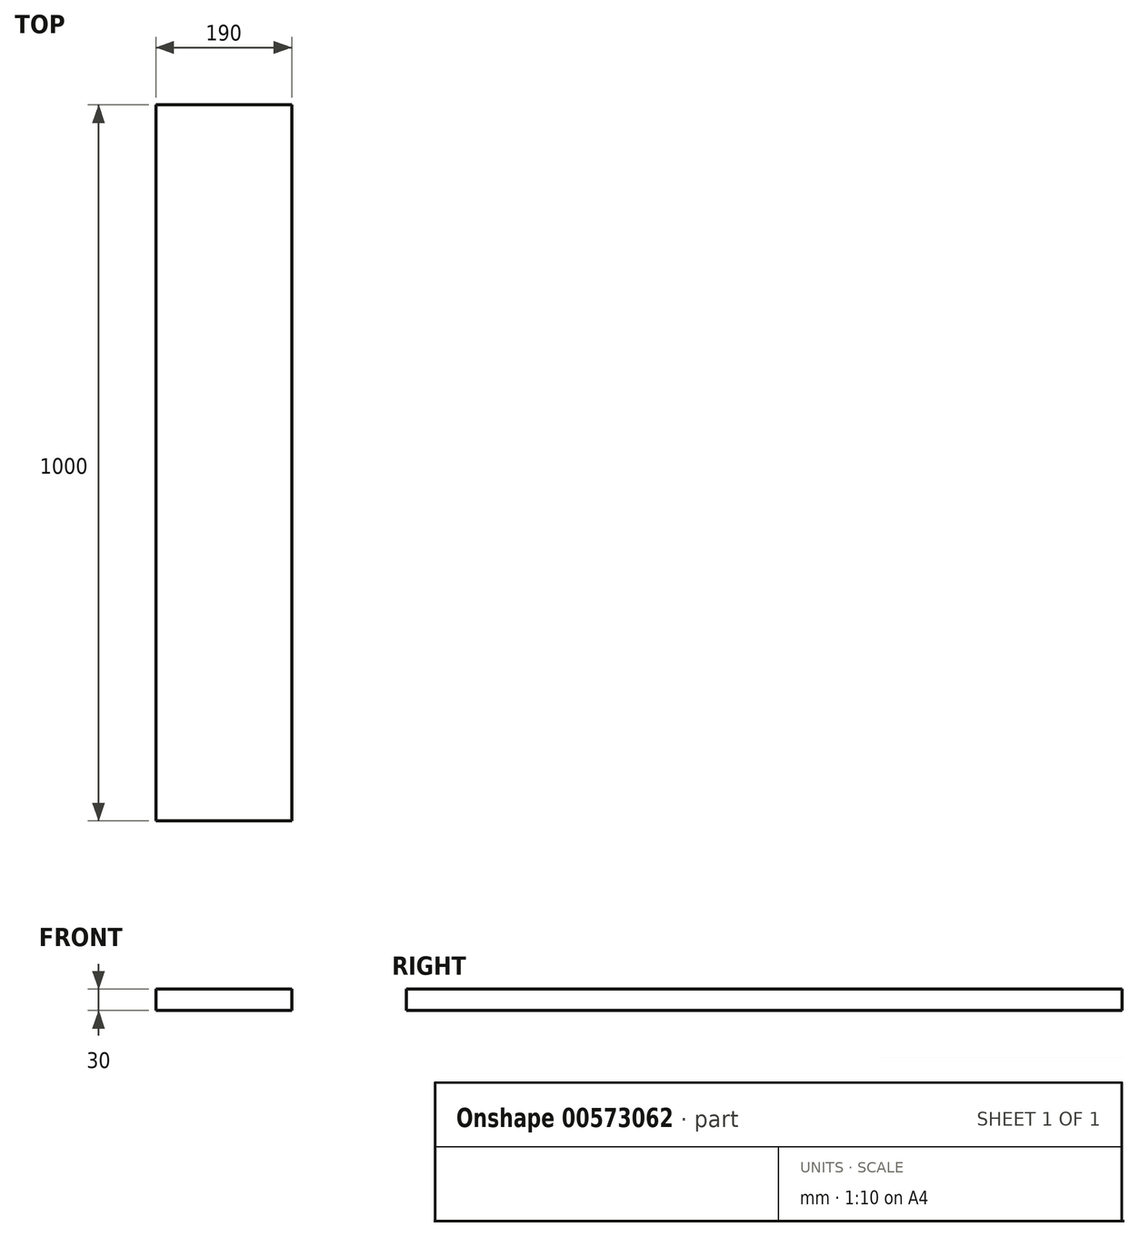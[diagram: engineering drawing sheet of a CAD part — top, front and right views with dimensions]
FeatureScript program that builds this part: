
annotation { "Feature Type Name" : "Feature", "Feature Type Description" : "" }
export const myFeature = defineFeature(function(context is Context, id is Id, definition is map)
    precondition{}
    {
        {
            var Q0;
            Q0=qCreatedBy(makeId("Front.planeOp"),FACE);
            var sketch = newSketch(context, id + "F0", { "sketchPlane" : qUnion([Q0])});
            skLineSegment(sketch, "E0.bottom", {"start": v(-50.1, 21.95) * mm, "end": v(139.9, 21.95) * mm});
            skLineSegment(sketch, "E0.top", {"start": v(-50.1, -8.05) * mm, "end": v(139.9, -8.05) * mm});
            skLineSegment(sketch, "E0.left", {"start": v(-50.1, 21.95) * mm, "end": v(-50.1, -8.05) * mm});
            skLineSegment(sketch, "E0.right", {"start": v(139.9, 21.95) * mm, "end": v(139.9, -8.05) * mm});
            skSolve(sketch);
        }
        {
            var Q0;
            Q0 = qSketchRegion(id + "F0", true);
            extrude(context, id + "F1", {"entities" : qUnion([Q0]), "depth" : 1000 * mm, "offsetDistance" : 25 * mm});
        }
    });
